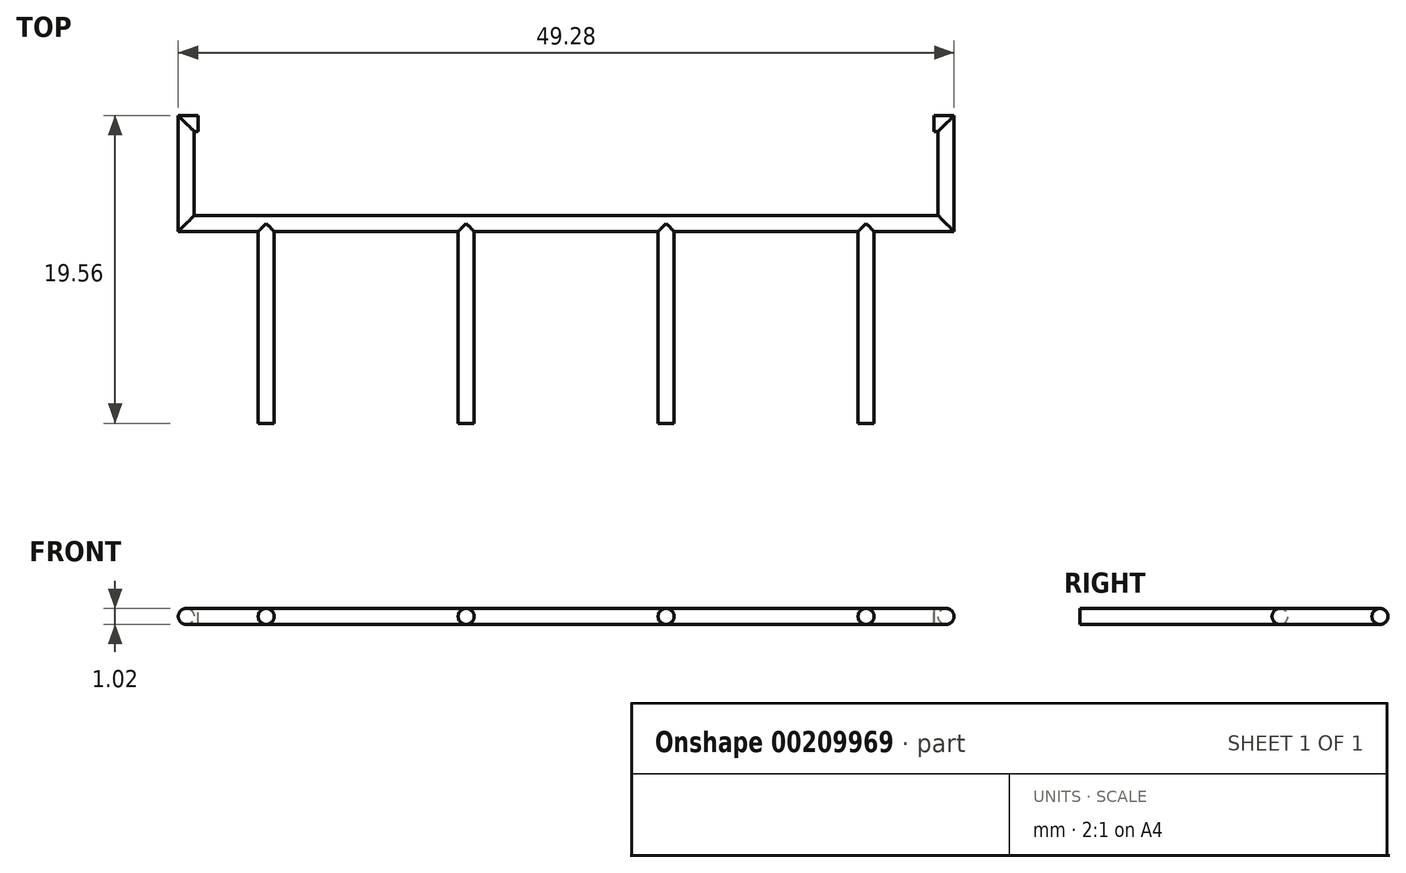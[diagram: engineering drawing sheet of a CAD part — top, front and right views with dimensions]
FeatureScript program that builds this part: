
annotation { "Feature Type Name" : "Feature", "Feature Type Description" : "" }
export const myFeature = defineFeature(function(context is Context, id is Id, definition is map)
    precondition{}
    {
        {
            var Q0;
            Q0=qCreatedBy(makeId("Top.planeOp"),FACE);
            var sketch = newSketch(context, id + "F0", { "sketchPlane" : qUnion([Q0])});
            skLineSegment(sketch, "E0", {"start": v(-19.05, 0) * mm, "end": v(-19.05, 12.7) * mm});
            skLineSegment(sketch, "E1", {"start": v(-19.05, 12.7) * mm, "end": v(19.05, 12.7) * mm});
            skLineSegment(sketch, "E2", {"start": v(19.05, 12.7) * mm, "end": v(19.05, 0) * mm});
            skLineSegment(sketch, "E3", {"start": v(-12.7, 12.7) * mm, "end": v(-12.7, 0) * mm});
            skLineSegment(sketch, "E4", {"start": v(12.7, 12.7) * mm, "end": v(12.7, 0) * mm});
            skPoint(sketch, "E5.endSnap0", {"position": v(0, 12.7) * mm});
            skLineSegment(sketch, "E6", {"start": v(-19.05, 12.7) * mm, "end": v(-25.4, 12.7) * mm});
            skLineSegment(sketch, "E7", {"start": v(-25.4, 12.7) * mm, "end": v(-25.4, 19.05) * mm});
            skLineSegment(sketch, "E8", {"start": v(-25.4, 19.05) * mm, "end": v(-23.37, 19.05) * mm});
            skLineSegment(sketch, "E9", {"start": v(19.05, 12.7) * mm, "end": v(25.4, 12.7) * mm});
            skLineSegment(sketch, "E10", {"start": v(25.4, 12.7) * mm, "end": v(25.4, 19.05) * mm});
            skLineSegment(sketch, "E11", {"start": v(25.4, 19.05) * mm, "end": v(23.37, 19.05) * mm});
            skSolve(sketch);
        }
        {
            var Q0;
            Q0=qCreatedBy(makeId("Front.planeOp"),FACE);
            var sketch = newSketch(context, id + "F1", { "sketchPlane" : qUnion([Q0])});
            skCircle(sketch, "E12", {"center": v(-19.05, 0) * mm, "radius": 0.5 * mm});
            skSolve(sketch);
        }
        {
            var Q0;
            Q0=makeQuery(id+"F1.imprint","IMPRINT",FACE,{"disambiguationData":[TD([[makeQuery(id+"F1.imprint","IMPRINT",EDGE,{"derivedFrom":sQuery(id+"F1.wireOp",EDGE,"E12")}),1.0]])]});
            var Q1;
            Q1=sQuery(id+"F0.wireOp",EDGE,"E0");
            var Q2;
            Q2=sQuery(id+"F0.wireOp",EDGE,"E1");
            var Q3;
            Q3=sQuery(id+"F0.wireOp",EDGE,"E2");
            sweep(context, id + "F2", {"profiles" : qUnion([Q0]), "path" : qUnion([Q1, Q2, Q3])});
        }
        {
            var Q0;
            Q0=qCreatedBy(makeId("Front.planeOp"),FACE);
            cPlane(context, id + "F3", {"entities" : qUnion([Q0]), "cplaneType" : CPlaneType.OFFSET, "offset" : 12.7 * mm, "oppositeDirection" : true, "width" : 152.4 * mm, "height" : 152.4 * mm});
        }
        {
            var Q0;
            Q0=qCreatedBy(id+"F3.planeOp",FACE);
            var sketch = newSketch(context, id + "F4", { "sketchPlane" : qUnion([Q0])});
            skCircle(sketch, "E13", {"center": v(-6.35, 0) * mm, "radius": 0.5 * mm});
            skCircle(sketch, "E14", {"center": v(6.35, 0) * mm, "radius": 0.5 * mm});
            skSolve(sketch);
        }
        {
            var Q0;
            Q0 = qSketchRegion(id + "F4", true);
            extrude(context, id + "F5", {"entities" : qUnion([Q0]), "operationType" : NewBodyOperationType.ADD, "depth" : 12.7 * mm});
        }
        {
            var Q0;
            Q0=qCreatedBy(makeId("Top.planeOp"),FACE);
            var sketch = newSketch(context, id + "F6", { "sketchPlane" : qUnion([Q0])});
            skLineSegment(sketch, "E15", {"start": v(-19.05, 12.7) * mm, "end": v(-24.13, 12.7) * mm});
            skLineSegment(sketch, "E16", {"start": v(-24.13, 12.7) * mm, "end": v(-24.13, 19.05) * mm});
            skLineSegment(sketch, "E17", {"start": v(-24.13, 19.05) * mm, "end": v(-23.37, 19.05) * mm});
            skLineSegment(sketch, "E18", {"start": v(19.05, 12.7) * mm, "end": v(24.13, 12.7) * mm});
            skLineSegment(sketch, "E19", {"start": v(24.13, 12.7) * mm, "end": v(24.13, 19.05) * mm});
            skLineSegment(sketch, "E20", {"start": v(24.13, 19.05) * mm, "end": v(23.37, 19.05) * mm});
            skLineSegment(sketch, "E21", {"start": v(-19.05, 12.7) * mm, "end": v(19.05, 12.7) * mm});
            skSolve(sketch);
        }
        {
            var Q0;
            Q0=qCreatedBy(makeId("Right.planeOp"),FACE);
            cPlane(context, id + "F7", {"entities" : qUnion([Q0]), "cplaneType" : CPlaneType.OFFSET, "offset" : 19.05 * mm, "width" : 152.4 * mm, "height" : 152.4 * mm});
        }
        {
            var Q0;
            Q0=qCreatedBy(id+"F7.planeOp",FACE);
            var sketch = newSketch(context, id + "F8", { "sketchPlane" : qUnion([Q0])});
            skCircle(sketch, "E22", {"center": v(12.7, 0) * mm, "radius": 0.5 * mm});
            skSolve(sketch);
        }
        {
            var Q0;
            Q0 = qSketchRegion(id + "F8", true);
            var Q1;
            Q1=sQuery(id+"F8.wireOp",EDGE,"E22");
            var Q2;
            Q2=sQuery(id+"F6.wireOp",EDGE,"E18");
            var Q3;
            Q3=sQuery(id+"F6.wireOp",EDGE,"E19");
            var Q4;
            Q4=sQuery(id+"F6.wireOp",EDGE,"E20");
            sweep(context, id + "F9", {"operationType" : NewBodyOperationType.ADD, "profiles" : qUnion([Q0]), "surfaceProfiles" : qUnion([Q1]), "path" : qUnion([Q2, Q3, Q4])});
        }
        {
            var Q0;
            Q0=qCreatedBy(makeId("Right.planeOp"),FACE);
            cPlane(context, id + "F10", {"entities" : qUnion([Q0]), "cplaneType" : CPlaneType.OFFSET, "offset" : 19.05 * mm, "oppositeDirection" : true, "width" : 152.4 * mm, "height" : 152.4 * mm});
        }
        {
            var Q0;
            Q0=qCreatedBy(id+"F10.planeOp",FACE);
            var sketch = newSketch(context, id + "F11", { "sketchPlane" : qUnion([Q0])});
            skCircle(sketch, "E23", {"center": v(12.7, 0) * mm, "radius": 0.5 * mm});
            skSolve(sketch);
        }
        {
            var Q0;
            Q0=qCreatedBy(makeId("Top.planeOp"),FACE);
            var sketch = newSketch(context, id + "F12", { "sketchPlane" : qUnion([Q0])});
            skLineSegment(sketch, "E24", {"start": v(-19.05, 12.7) * mm, "end": v(-24.13, 12.7) * mm});
            skLineSegment(sketch, "E25", {"start": v(-24.13, 12.7) * mm, "end": v(-24.13, 19.05) * mm});
            skLineSegment(sketch, "E26", {"start": v(-24.13, 19.05) * mm, "end": v(-23.37, 19.05) * mm});
            skSolve(sketch);
        }
        {
            var Q0;
            Q0 = qSketchRegion(id + "F11", true);
            var Q1;
            Q1 = qConstructionFilter(qBodyType(qCreatedBy(id + "F12" ,EDGE), BodyType.WIRE), ConstructionObject.NO);
            sweep(context, id + "F13", {"operationType" : NewBodyOperationType.ADD, "profiles" : qUnion([Q0]), "path" : qUnion([Q1])});
        }
    });
